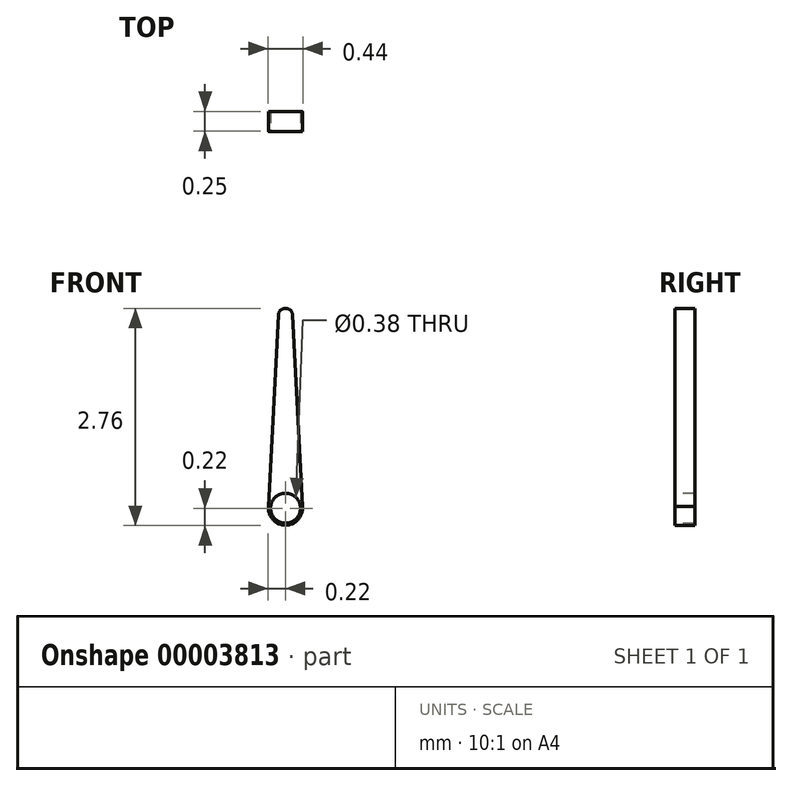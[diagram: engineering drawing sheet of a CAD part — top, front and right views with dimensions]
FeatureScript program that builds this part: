
annotation { "Feature Type Name" : "Feature", "Feature Type Description" : "" }
export const myFeature = defineFeature(function(context is Context, id is Id, definition is map)
    precondition{}
    {
        {
            var Q0;
            Q0=qCreatedBy(makeId("Front.planeOp"),FACE);
            var sketch = newSketch(context, id + "F0", { "sketchPlane" : qUnion([Q0])});
            skArc(sketch, "E0", {"start": v(-0.21, 0.04) * mm, "mid": v(0, -0.22) * mm, "end": v(0.21, 0.04) * mm});
            skLineSegment(sketch, "E1", {"start": v(-0.22, 0) * mm, "end": v(-0.21, 0.04) * mm});
            skLineSegment(sketch, "E2", {"start": v(0, 2.54) * mm, "end": v(0, 0) * mm, "construction": true});
            skLineSegment(sketch, "E3.0.MirrorCS", {"start": v(0.22, 0) * mm, "end": v(0.21, 0.04) * mm});
            skLineSegment(sketch, "E4", {"start": v(-0.22, 0) * mm, "end": v(-0.1, 2.45) * mm});
            skLineSegment(sketch, "E5", {"start": v(0, 2.54) * mm, "end": v(0, 2.54) * mm});
            skPoint(sketch, "E6.visualSharp", {"position": v(-0.09, 2.54) * mm});
            skArc(sketch, "E6.filletArc", {"start": v(0, 2.54) * mm, "mid": v(-0.06, 2.52) * mm, "end": v(-0.1, 2.45) * mm});
            skLineSegment(sketch, "E7.0.MirrorCS", {"start": v(0.22, 0) * mm, "end": v(0.1, 2.45) * mm});
            skArc(sketch, "E8.0.MirrorCS", {"start": v(0, 2.54) * mm, "mid": v(0.06, 2.52) * mm, "end": v(0.1, 2.45) * mm});
            skSolve(sketch);
        }
        {
            var Q0;
            Q0 = qSketchRegion(id + "F0", true);
            extrude(context, id + "F1", {"entities" : qUnion([Q0]), "depth" : 0.25 * mm});
        }
        {
            var Q0;
            Q0=makeQuery(id+"F1.opExtrude","CAP_FACE",FACE,{"disambiguationData":[OSD([sQuery(id+"F0.wireOp",EDGE,"E0"),sQuery(id+"F0.wireOp",EDGE,"E4"),sQuery(id+"F0.wireOp",EDGE,"E7.0.MirrorCS"),sQuery(id+"F0.wireOp",EDGE,"E8.0.MirrorCS")])],"isStart":false});
            var sketch = newSketch(context, id + "F2", { "sketchPlane" : qUnion([Q0])});
            skCircle(sketch, "E9", {"center": v(0, 0) * mm, "radius": 0.2 * mm});
            skSolve(sketch);
        }
        {
            var Q0;
            Q0=makeQuery(id+"F2.imprint","IMPRINT",FACE,{"disambiguationData":[TD([[makeQuery(id+"F2.imprint","IMPRINT",EDGE,{"derivedFrom":sQuery(id+"F2.wireOp",EDGE,"E9")}),1.0]])]});
            extrude(context, id + "F3", {"entities" : qUnion([Q0]), "operationType" : NewBodyOperationType.REMOVE, "endBound" : BoundingType.THROUGH_ALL, "oppositeDirection" : true, "depth" : 25.4 * mm});
        }
    });
